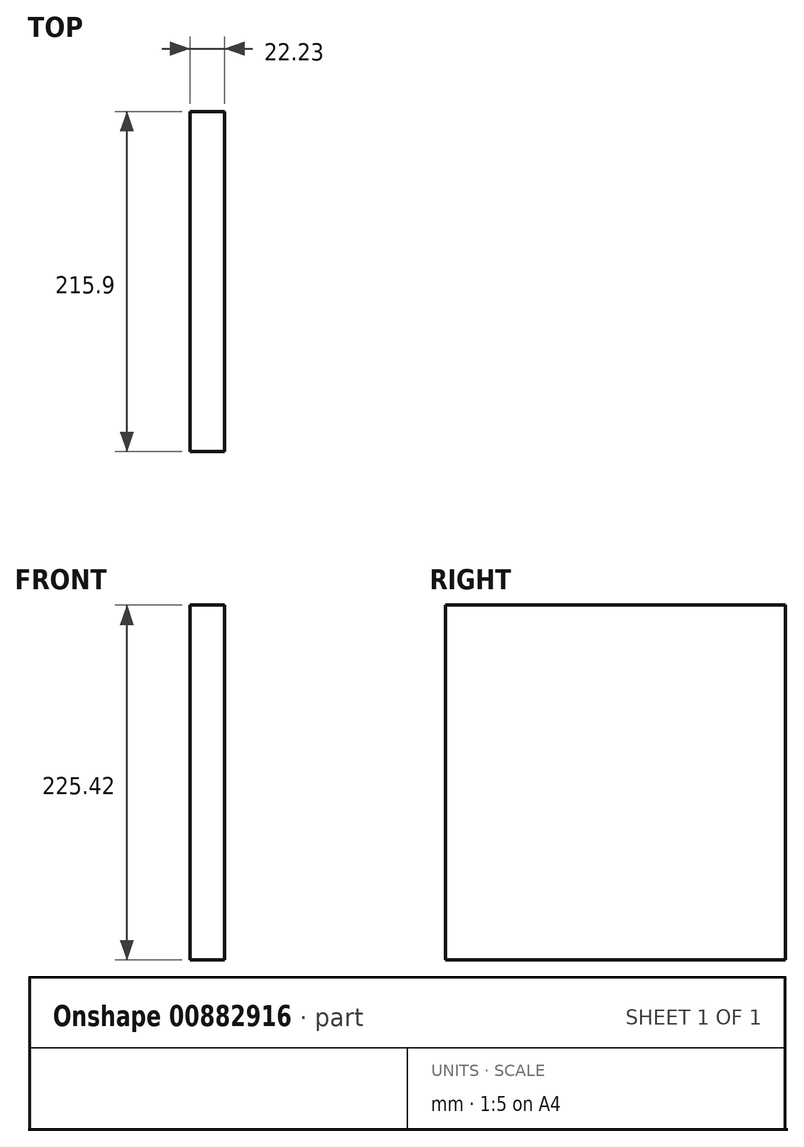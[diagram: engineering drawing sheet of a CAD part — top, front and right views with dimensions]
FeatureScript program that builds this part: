
annotation { "Feature Type Name" : "Feature", "Feature Type Description" : "" }
export const myFeature = defineFeature(function(context is Context, id is Id, definition is map)
    precondition{}
    {
        {
            var Q0;
            Q0=qCreatedBy(makeId("Right.planeOp"),FACE);
            var sketch = newSketch(context, id + "F0", { "sketchPlane" : qUnion([Q0])});
            skLineSegment(sketch, "E0.bottom", {"start": v(0, 0) * mm, "end": v(215.9, 0) * mm});
            skLineSegment(sketch, "E0.top", {"start": v(0, -225.43) * mm, "end": v(215.9, -225.43) * mm});
            skLineSegment(sketch, "E0.left", {"start": v(0, 0) * mm, "end": v(0, -225.43) * mm});
            skLineSegment(sketch, "E0.right", {"start": v(215.9, 0) * mm, "end": v(215.9, -225.43) * mm});
            skSolve(sketch);
        }
        {
            var Q0;
            Q0=makeQuery(id+"F0.imprint","IMPRINT",FACE,{"disambiguationData":[TD([[makeQuery(id+"F0.imprint","IMPRINT",EDGE,{"derivedFrom":sQuery(id+"F0.wireOp",EDGE,"E0.bottom")}),-1.0]])]});
            extrude(context, id + "F1", {"entities" : qUnion([Q0]), "depth" : 22.22 * mm, "offsetDistance" : 25.4 * mm});
        }
    });
